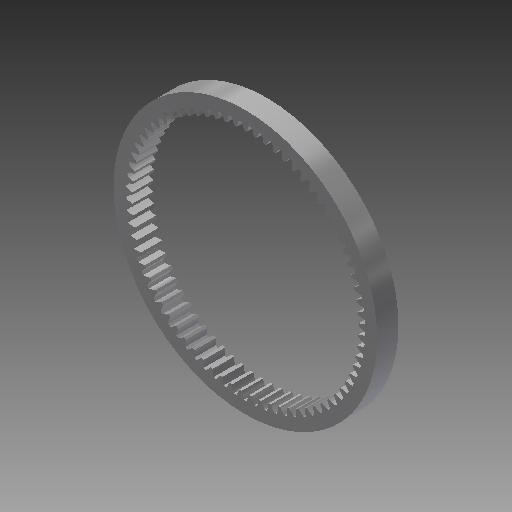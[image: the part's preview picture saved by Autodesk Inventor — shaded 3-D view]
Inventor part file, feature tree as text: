
AUTODESK INVENTOR PART (.ipt)
format: ipt  version: 2019 (Build 230136000, 136)  size: 459,264 bytes
history: native  units: mm (DEFAULTED — no unit token found)
features: plane x3, other x3, sketch x2, extrude x1
ambient origin geometry x8: Origin, YZ Plane, XZ Plane, XY Plane, X Axis, Y Axis, Z Axis, Center Point
bodies: Solid1 (feature_tree)
feature tree (9):
  extrude  "Extrusion1"  Depth=10.0mm TaperAngle=0.0deg
  plane  "Work Plane2"
  plane  "Work Plane8"
  plane  "Work Plane9"
  other  "正齒輪"
  sketch  "Sketch1"  dims[d0=123.430444mm d1=10.0mm d2=0.0mm]
  sketch  "Sketch2"  dims[d3=107.919785mm d4=10.0mm d5=0.0mm d16=37.698007mm d17=0.0mm d34=0.430355mm d39=0.0mm d45=0.0mm d47=37.698007mm d50=0.0mm d51=0.0mm d52=37.698007mm]
  other  "Srf1"
  other  "節圓直徑"
